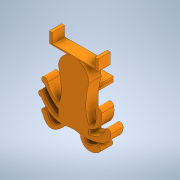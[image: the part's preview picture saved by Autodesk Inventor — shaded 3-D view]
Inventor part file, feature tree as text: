
AUTODESK INVENTOR PART (.ipt)
format: ipt  version: 2020 (Build 240168000, 168)  size: 243,712 bytes
history: native  units: mm
features: extrude x4, sketch x4
ambient origin geometry x8: Origin, YZ Plane, XZ Plane, XY Plane, X Axis, Y Axis, Z Axis, Center Point
bodies: Solid1 (feature_tree)
feature tree (8):
  extrude  "Extrusion1"  Depth=40.0mm
  extrude  "Belt box"  Depth=5.0mm
  extrude  "belt cut out"  Depth=5.0mm
  extrude  "Extrusion4"  Depth=8.0mm
  sketch  "Sketch2"  dims[d6=40.0mm d7=25.0mm]
  sketch  "Sketch3"  dims[d8=5.0mm d9=5.0mm]
  sketch  "Sketch4"  dims[d10=5.0mm d11=5.0mm]
  sketch  "Sketch5"  dims[d12=5.0mm d13=5.0mm d14=10.0mm d15=0.0mm d16=15.0mm d17=20.0mm d18=15.0mm d19=0.0mm d20=8.0mm d21=8.0mm d22=15.0mm d23=0.7mm d24=15.0mm d25=27.5mm d26=15.0mm d27=0.0mm d29=1.0mm d30=25.0mm d31=25.0mm d33=8.0mm d34=8.0mm d36=10.0mm d37=0.0mm]
